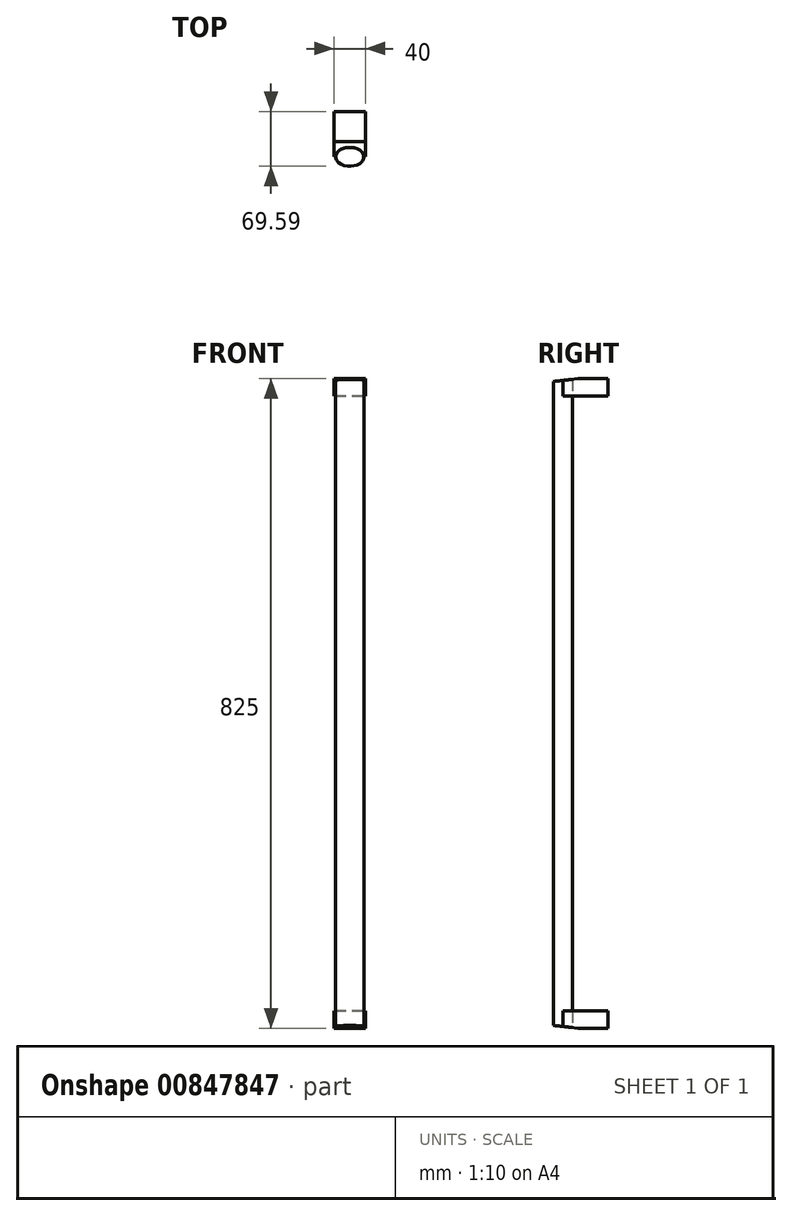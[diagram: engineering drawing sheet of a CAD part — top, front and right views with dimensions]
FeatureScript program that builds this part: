
annotation { "Feature Type Name" : "Feature", "Feature Type Description" : "" }
export const myFeature = defineFeature(function(context is Context, id is Id, definition is map)
    precondition{}
    {
        {
            var Q0;
            Q0=qCreatedBy(makeId("Top.planeOp"),FACE);
            var sketch = newSketch(context, id + "F0", { "sketchPlane" : qUnion([Q0])});
            skEllipse(sketch, "E0", {"center": v(0, 0) * mm, "majorRadius": 17.97 * mm, "minorRadius": 11.96 * mm, "majorAxis": v(-1, 0)});
            skSolve(sketch);
        }
        {
            var Q0;
            Q0=qCreatedBy(makeId("Top.planeOp"),FACE);
            cPlane(context, id + "F1", {"entities" : qUnion([Q0]), "cplaneType" : CPlaneType.OFFSET, "offset" : 390.52 * mm, "width" : 152.4 * mm, "height" : 152.4 * mm});
        }
        {
            var Q0;
            Q0=qCreatedBy(id+"F1.planeOp",FACE);
            var sketch = newSketch(context, id + "F2", { "sketchPlane" : qUnion([Q0])});
            skFitSpline(sketch, "E1.0", {"points": [v(-19.93, 1.48) * mm, v(-20.04, 0) * mm, v(-19.93, -1.48) * mm, v(-19.5, -3.4) * mm, v(-18.66, -5.24) * mm, v(-17.46, -6.92) * mm, v(-16.04, -8.5) * mm, v(-13.91, -10.22) * mm, v(-11.39, -11.6) * mm, v(-9.16, -12.49) * mm, v(-6.84, -13.22) * mm, v(-4.4, -13.7) * mm, v(-1.9, -13.95) * mm, v(0, -14.02) * mm, v(1.9, -13.95) * mm, v(4.4, -13.7) * mm, v(6.84, -13.22) * mm, v(9.16, -12.49) * mm, v(11.39, -11.6) * mm, v(13.91, -10.22) * mm, v(16.04, -8.5) * mm, v(17.46, -6.92) * mm, v(18.66, -5.24) * mm, v(19.5, -3.4) * mm, v(19.93, -1.48) * mm, v(20.04, 0) * mm, v(19.93, 1.48) * mm, v(19.5, 3.4) * mm, v(18.66, 5.24) * mm, v(17.46, 6.92) * mm, v(16.04, 8.5) * mm, v(13.91, 10.22) * mm, v(11.39, 11.6) * mm, v(9.16, 12.49) * mm, v(6.84, 13.22) * mm, v(4.4, 13.7) * mm, v(1.9, 13.95) * mm, v(0, 14.02) * mm, v(-1.9, 13.95) * mm, v(-4.4, 13.7) * mm, v(-6.84, 13.22) * mm, v(-9.16, 12.49) * mm, v(-11.39, 11.6) * mm, v(-13.91, 10.22) * mm, v(-16.04, 8.5) * mm, v(-17.46, 6.92) * mm, v(-18.66, 5.24) * mm, v(-19.5, 3.4) * mm, v(-19.93, 1.48) * mm, v(-20.04, 0) * mm, v(-19.93, -1.48) * mm, v(-19.93, 1.48) * mm]});
            skLineSegment(sketch, "E2.bottom", {"start": v(-20, 0) * mm, "end": v(20, 0) * mm});
            skLineSegment(sketch, "E2.top", {"start": v(-20, 57.63) * mm, "end": v(20, 57.63) * mm});
            skLineSegment(sketch, "E2.left", {"start": v(-20, 0) * mm, "end": v(-20, 57.63) * mm});
            skLineSegment(sketch, "E2.right", {"start": v(20, 0) * mm, "end": v(20, 57.63) * mm});
            skLineSegment(sketch, "E3", {"start": v(0, 14) * mm, "end": v(0, -14) * mm, "construction": true});
            skSolve(sketch);
        }
        {
            var Q0;
            Q0 = qSketchRegion(id + "F2", true);
            extrude(context, id + "F3", {"entities" : qUnion([Q0]), "depth" : 21.97 * mm, "offsetDistance" : 25.4 * mm});
        }
        {
            var Q0;
            Q0=qCreatedBy(makeId("Right.planeOp"),FACE);
            var sketch = newSketch(context, id + "F4", { "sketchPlane" : qUnion([Q0])});
            skLineSegment(sketch, "E4", {"start": v(19.53, 412.5) * mm, "end": v(-14, 412.5) * mm});
            skLineSegment(sketch, "E5", {"start": v(-14, 412.5) * mm, "end": v(-14, 408.86) * mm});
            skLineSegment(sketch, "E6", {"start": v(-14, 408.86) * mm, "end": v(19.53, 412.5) * mm});
            skSolve(sketch);
        }
        {
            var Q0;
            Q0 = qSketchRegion(id + "F4", true);
            extrude(context, id + "F5", {"entities" : qUnion([Q0]), "operationType" : NewBodyOperationType.REMOVE, "endBound" : BoundingType.THROUGH_ALL, "oppositeDirection" : true, "depth" : 25.4 * mm, "offsetDistance" : 25.4 * mm, "hasSecondDirection" : true, "secondDirectionBound" : SecondDirectionBoundingType.THROUGH_ALL, "secondDirectionOppositeDirection" : false, "secondDirectionDepth" : 25.4 * mm});
        }
        {
            var Q0;
            Q0=makeQuery(id+"F3.opExtrude","SWEPT_BODY",BODY,{"disambiguationData":[OSD([sQuery(id+"F2.wireOp",EDGE,"E1.0"),sQuery(id+"F2.wireOp",EDGE,"E2.top"),sQuery(id+"F2.wireOp",EDGE,"E2.left"),sQuery(id+"F2.wireOp",EDGE,"E2.right")])]});
            var Q1;
            Q1=qCreatedBy(makeId("Top.planeOp"),FACE);
            mirror(context, id + "F6", {"entities" : qUnion([Q0]), "mirrorPlane" : qUnion([Q1])});
        }
        {
            var Q0;
            Q0=makeQuery(id+"F0.imprint","IMPRINT",FACE,{"disambiguationData":[TD([[makeQuery(id+"F0.imprint","IMPRINT",EDGE,{"derivedFrom":sQuery(id+"F0.wireOp",EDGE,"E0")}),1.0]])]});
            var Q1;
            Q1=makeQuery(id+"F5.boolean.opBoolean","COPY",FACE,{"derivedFrom":makeQuery(id+"F5.opExtrude","SWEPT_FACE",FACE,{"disambiguationData":[OSD([sQuery(id+"F4.wireOp",EDGE,"E6")])]})});
            var Q2;
            Q2=makeQuery(id+"F6.opPattern","COPY",FACE,{"derivedFrom":makeQuery(id+"F5.boolean.opBoolean","COPY",FACE,{"derivedFrom":makeQuery(id+"F5.opExtrude","SWEPT_FACE",FACE,{"disambiguationData":[OSD([sQuery(id+"F4.wireOp",EDGE,"E6")])]})}),"instanceName":"1"});
            extrude(context, id + "F7", {"entities" : qUnion([Q0]), "endBound" : BoundingType.UP_TO_SURFACE, "depth" : 25.4 * mm, "endBoundEntityFace" : qUnion([Q1]), "hasOffset" : true, "offsetDistance" : 0.03 * mm, "offsetOppositeDirection" : true, "hasSecondDirection" : true, "secondDirectionBound" : SecondDirectionBoundingType.UP_TO_SURFACE, "secondDirectionOppositeDirection" : true, "secondDirectionDepth" : 25.4 * mm, "secondDirectionBoundEntityFace" : qUnion([Q2]), "hasSecondDirectionOffset" : true, "secondDirectionOffsetDistance" : 0.03 * mm, "secondDirectionOffsetOppositeDirection" : true});
        }
        {
            var Q0;
            Q0=makeQuery(id+"F7.opExtrude","SWEPT_BODY",BODY,{"disambiguationData":[OSD([sQuery(id+"F0.wireOp",EDGE,"E0")])]});
            var Q1;
            Q1=makeQuery(id+"F6.opPattern","COPY",BODY,{"derivedFrom":makeQuery(id+"F3.opExtrude","SWEPT_BODY",BODY,{"disambiguationData":[OSD([sQuery(id+"F2.wireOp",EDGE,"E1.0"),sQuery(id+"F2.wireOp",EDGE,"E2.top"),sQuery(id+"F2.wireOp",EDGE,"E2.left"),sQuery(id+"F2.wireOp",EDGE,"E2.right")])]}),"instanceName":"1"});
            var Q2;
            Q2=makeQuery(id+"F3.opExtrude","SWEPT_BODY",BODY,{"disambiguationData":[OSD([sQuery(id+"F2.wireOp",EDGE,"E1.0"),sQuery(id+"F2.wireOp",EDGE,"E2.top"),sQuery(id+"F2.wireOp",EDGE,"E2.left"),sQuery(id+"F2.wireOp",EDGE,"E2.right")])]});
            booleanBodies(context, id + "F8", {"operationType" : BooleanOperationType.SUBTRACTION, "tools" : qUnion([Q0]), "targets" : qUnion([Q1, Q2]), "keepTools" : true});
        }
    });
